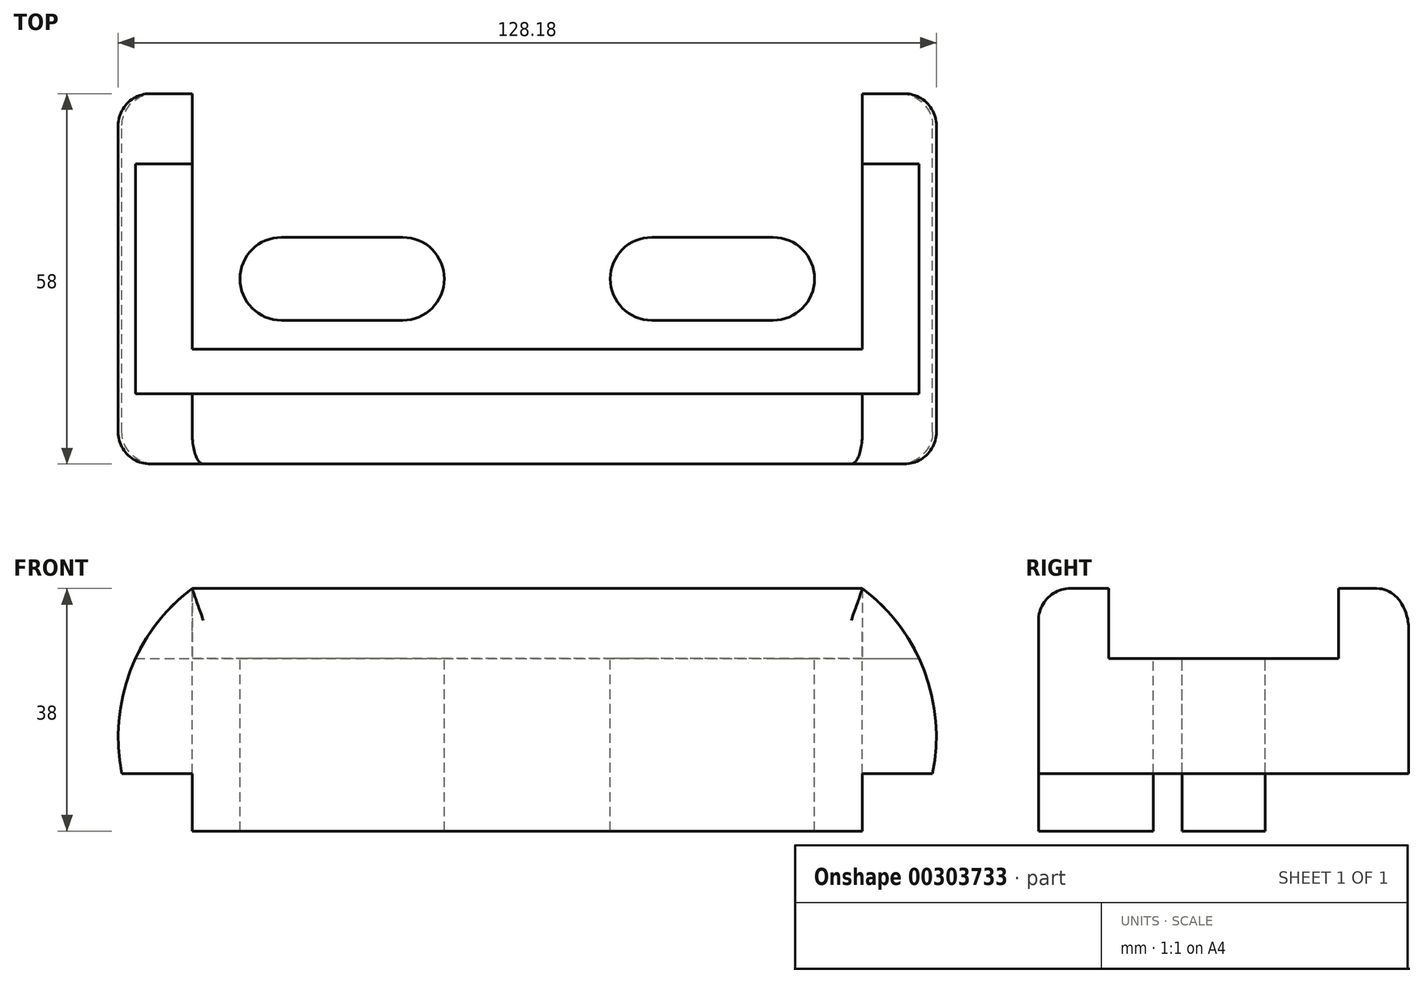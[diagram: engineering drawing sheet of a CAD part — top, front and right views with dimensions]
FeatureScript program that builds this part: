
annotation { "Feature Type Name" : "Feature", "Feature Type Description" : "" }
export const myFeature = defineFeature(function(context is Context, id is Id, definition is map)
    precondition{}
    {
        {
            var Q0;
            Q0=qCreatedBy(makeId("Front.planeOp"),FACE);
            var sketch = newSketch(context, id + "F0", { "sketchPlane" : qUnion([Q0])});
            skLineSegment(sketch, "E0", {"start": v(0, 0) * mm, "end": v(105, 0) * mm});
            skLineSegment(sketch, "E1", {"start": v(0, 0) * mm, "end": v(0, 9) * mm});
            skLineSegment(sketch, "E2", {"start": v(0, 9) * mm, "end": v(-11, 9) * mm});
            skLineSegment(sketch, "E3", {"start": v(105, 0) * mm, "end": v(105, 9) * mm});
            skLineSegment(sketch, "E4", {"start": v(105, 9) * mm, "end": v(116, 9) * mm});
            skLineSegment(sketch, "E5", {"start": v(0, 38) * mm, "end": v(105, 38) * mm});
            skArc(sketch, "E6", {"start": v(0, 38) * mm, "mid": v(-9.7, 25.1) * mm, "end": v(-11, 9) * mm});
            skArc(sketch, "E7", {"start": v(116, 9) * mm, "mid": v(114.7, 25.1) * mm, "end": v(105, 38) * mm});
            skSolve(sketch);
        }
        {
            var Q0;
            Q0 = qSketchRegion(id + "F0", true);
            extrude(context, id + "F1", {"entities" : qUnion([Q0]), "endBound" : BoundingType.SYMMETRIC, "depth" : 58 * mm});
        }
        {
            var Q0;
            Q0=makeQuery(id+"F1.opExtrude","SWEPT_FACE",FACE,{"disambiguationData":[OSD([sQuery(id+"F0.wireOp",EDGE,"E5")])]});
            var sketch = newSketch(context, id + "F2", { "sketchPlane" : qUnion([Q0])});
            skLineSegment(sketch, "E8", {"start": v(0, -18) * mm, "end": v(105, -18) * mm});
            skLineSegment(sketch, "E9", {"start": v(0, -11) * mm, "end": v(105, -11) * mm});
            skLineSegment(sketch, "E10", {"start": v(14, 0) * mm, "end": v(33, 0) * mm, "construction": true});
            skLineSegment(sketch, "E11", {"start": v(72, 0) * mm, "end": v(91, 0) * mm, "construction": true});
            skArc(sketch, "E12.0.startCap", {"start": v(14, -6.5) * mm, "mid": v(7.5, 0) * mm, "end": v(14, 6.5) * mm});
            skArc(sketch, "E12.0.endCap", {"start": v(33, 6.5) * mm, "mid": v(39.5, 0) * mm, "end": v(33, -6.5) * mm});
            skLineSegment(sketch, "E12.0.left", {"start": v(14, 6.5) * mm, "end": v(33, 6.5) * mm});
            skLineSegment(sketch, "E12.0.right", {"start": v(14, -6.5) * mm, "end": v(33, -6.5) * mm});
            skArc(sketch, "E12.1.startCap", {"start": v(72, -6.5) * mm, "mid": v(65.5, 0) * mm, "end": v(72, 6.5) * mm});
            skArc(sketch, "E12.1.endCap", {"start": v(91, 6.5) * mm, "mid": v(97.5, 0) * mm, "end": v(91, -6.5) * mm});
            skLineSegment(sketch, "E12.1.left", {"start": v(72, 6.5) * mm, "end": v(91, 6.5) * mm});
            skLineSegment(sketch, "E12.1.right", {"start": v(72, -6.5) * mm, "end": v(91, -6.5) * mm});
            skLineSegment(sketch, "E13", {"start": v(0, -11) * mm, "end": v(0, -18) * mm});
            skLineSegment(sketch, "E14", {"start": v(105, -11) * mm, "end": v(105, -18) * mm});
            skSolve(sketch);
        }
        {
            var Q0;
            Q0=makeQuery(id+"F2.imprint","IMPRINT",FACE,{"disambiguationData":[TD([[makeQuery(id+"F2.imprint","IMPRINT",EDGE,{"derivedFrom":sQuery(id+"F2.wireOp",EDGE,"E12.0.startCap")}),-1.0]])]});
            var Q1;
            Q1=makeQuery(id+"F2.imprint","IMPRINT",FACE,{"disambiguationData":[TD([[makeQuery(id+"F2.imprint","IMPRINT",EDGE,{"derivedFrom":sQuery(id+"F2.wireOp",EDGE,"E12.1.startCap")}),-1.0]])]});
            extrude(context, id + "F3", {"entities" : qUnion([Q0, Q1]), "operationType" : NewBodyOperationType.REMOVE, "endBound" : BoundingType.THROUGH_ALL, "oppositeDirection" : true, "depth" : 25 * mm});
        }
        {
            var Q0;
            Q0=qCreatedBy(makeId("Front.planeOp"),FACE);
            var sketch = newSketch(context, id + "F4", { "sketchPlane" : qUnion([Q0])});
            skArc(sketch, "E15", {"start": v(0, 38) * mm, "mid": v(-5.13, 33.05) * mm, "end": v(-8.9, 27) * mm});
            skArc(sketch, "E16", {"start": v(113.9, 27) * mm, "mid": v(110.13, 33.05) * mm, "end": v(105, 38) * mm});
            skLineSegment(sketch, "E17", {"start": v(0, 38) * mm, "end": v(105, 38) * mm});
            skLineSegment(sketch, "E18", {"start": v(-8.9, 27) * mm, "end": v(113.9, 27) * mm});
            skSolve(sketch);
        }
        {
            var Q0;
            Q0 = qSketchRegion(id + "F4", true);
            extrude(context, id + "F5", {"entities" : qUnion([Q0]), "operationType" : NewBodyOperationType.REMOVE, "endBound" : BoundingType.SYMMETRIC, "depth" : 36 * mm});
        }
        {
            var Q0;
            Q0=makeQuery(id+"F1.opExtrude","CAP_EDGE",EDGE,{"disambiguationData":[OSD([sQuery(id+"F0.wireOp",EDGE,"E7")])],"isStart":true});
            var Q1;
            Q1=makeQuery(id+"F1.opExtrude","CAP_EDGE",EDGE,{"disambiguationData":[OSD([sQuery(id+"F0.wireOp",EDGE,"E5")])],"isStart":true});
            var Q2;
            Q2=makeQuery(id+"F1.opExtrude","CAP_EDGE",EDGE,{"disambiguationData":[OSD([sQuery(id+"F0.wireOp",EDGE,"E6")])],"isStart":true});
            var Q3;
            Q3=makeQuery(id+"F1.opExtrude","CAP_EDGE",EDGE,{"disambiguationData":[OSD([sQuery(id+"F0.wireOp",EDGE,"E7")])],"isStart":false});
            var Q4;
            Q4=makeQuery(id+"F1.opExtrude","CAP_EDGE",EDGE,{"disambiguationData":[OSD([sQuery(id+"F0.wireOp",EDGE,"E5")])],"isStart":false});
            var Q5;
            Q5=makeQuery(id+"F1.opExtrude","CAP_EDGE",EDGE,{"disambiguationData":[OSD([sQuery(id+"F0.wireOp",EDGE,"E6")])],"isStart":false});
            fillet(context, id + "F6", {"entities" : qUnion([Q0, Q1, Q2, Q3, Q4, Q5]), "radius" : 5 * mm, "tangentPropagation" : true, "allowEdgeOverflow" : false});
        }
    });
